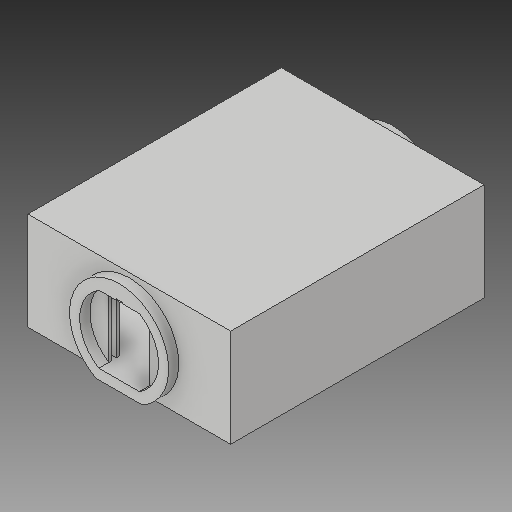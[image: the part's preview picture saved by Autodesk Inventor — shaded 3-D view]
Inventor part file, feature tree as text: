
AUTODESK INVENTOR PART (.ipt)
format: ipt  version: 2017 (Build 210142000, 142)  size: 275,968 bytes
history: native  units: in
note: dims shown in document units (in); Inventor stores cm internally (conversion verified against a paired STEP export)
features: extrude x9, sketch x7, mirror x3, other x1
ambient origin geometry x8: Origin, YZ Plane, XZ Plane, XY Plane, X Axis, Y Axis, Z Axis, Center Point
bodies: Solid1 (feature_tree), Solid2 (feature_tree)
feature tree (20):
  extrude  "floor"  Depth=25.0in
  extrude  "walls"  Depth=1.0in
  extrude  "doorframe"  Depth=1.0in
  extrude  "ceiling"  Depth=8.6667in TaperAngle=0.0deg
  extrude  "left door slot"  Depth=6.6667in
  mirror  "mirror door slot"
  mirror  "right door slot"
  sketch  "Sketch10"  dims[d20=8.6667in d21=0.0in d22=1.0in d23=0.0in]
  extrude  "corridor connect"  Depth=1.0in TaperAngle=0.0deg
  sketch  "Sketch11"  dims[d24=0.25in d25=0.5in d26=2.0in d27=0.0in d28=6.6667in d37=6.6667in d38=4.0in d39=1.0in d40=1.0in d41=0.0in d42=0.5833in d43=0.0625in d44=0.0625in d45=0.125in d46=0.25in d47=0.125in d48=45.0deg d49=0.0892in d50=0.0884in d51=1.0in d52=0.0in d53=1.0in d54=0.0in d55=1.0in d56=0.0in]
  extrude  "light"  Depth=0.5in
  extrude  "into wall light cut"  Depth=2.0in TaperAngle=0.0deg
  extrude  "into wall light join"  Depth=6.6667in
  other  "middle of the room"
  mirror  "Mirror connection for starting door"
  sketch  "Sketch1"  dims[d0=20.0in d1=25.0in]
  sketch  "Sketch4"  dims[d2=1.0in d3=0.0in d11=1.0in]
  sketch  "Sketch5"  dims[d12=1.0in d13=1.0in]
  sketch  "Sketch7"  dims[d14=1.0in d15=8.6667in d16=0.0in]
  sketch  "Sketch8"  dims[d17=2.0in d18=6.6667in]
